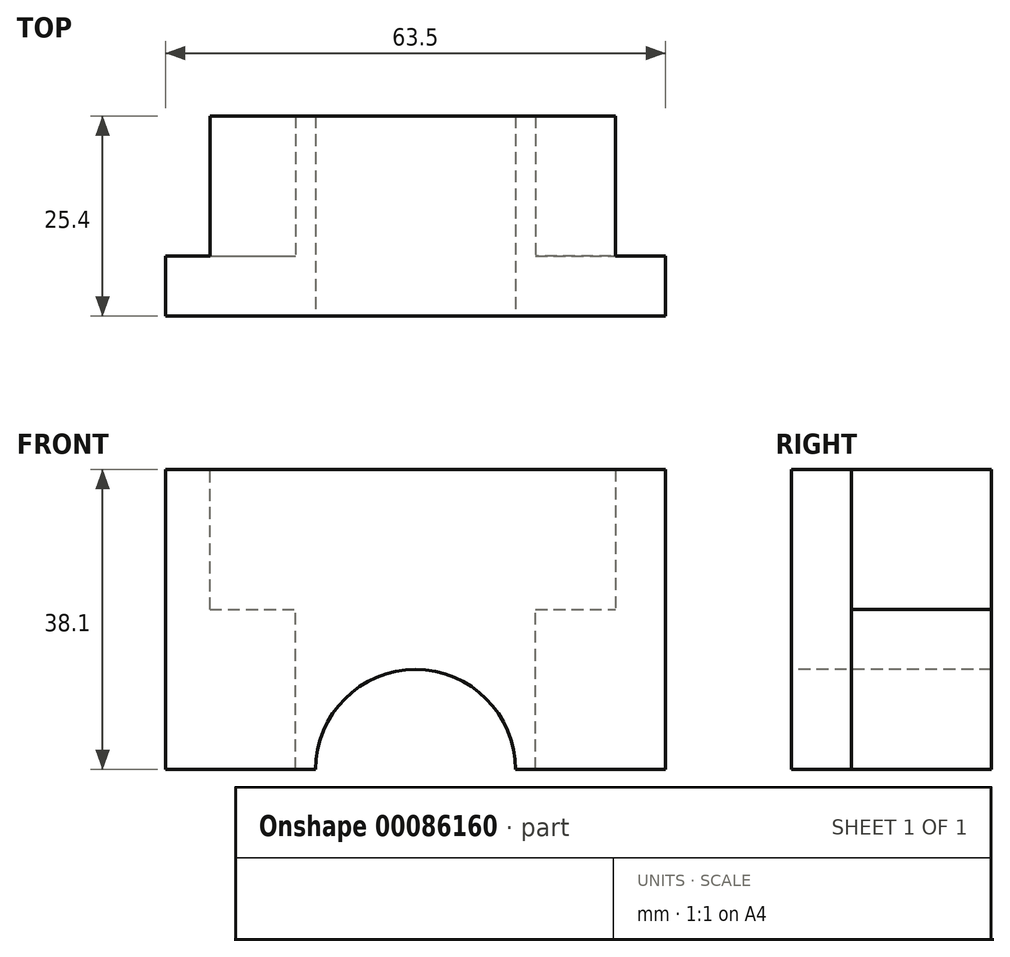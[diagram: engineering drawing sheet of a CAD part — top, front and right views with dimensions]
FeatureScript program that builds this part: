
annotation { "Feature Type Name" : "Feature", "Feature Type Description" : "" }
export const myFeature = defineFeature(function(context is Context, id is Id, definition is map)
    precondition{}
    {
        {
            var Q0;
            Q0=qCreatedBy(makeId("Front.planeOp"),FACE);
            var sketch = newSketch(context, id + "F0", { "sketchPlane" : qUnion([Q0])});
            skLineSegment(sketch, "E0", {"start": v(31.13, 18.61) * mm, "end": v(-32.37, 18.61) * mm});
            skLineSegment(sketch, "E1", {"start": v(-32.37, 18.61) * mm, "end": v(-32.37, -19.49) * mm});
            skLineSegment(sketch, "E2", {"start": v(-32.37, -19.49) * mm, "end": v(31.13, -19.49) * mm});
            skLineSegment(sketch, "E3", {"start": v(31.13, 18.61) * mm, "end": v(31.13, -19.49) * mm});
            skSolve(sketch);
        }
        {
            var Q0;
            Q0=makeQuery(id+"F0.imprint","IMPRINT",FACE,{"disambiguationData":[TD([[makeQuery(id+"F0.imprint","IMPRINT",EDGE,{"derivedFrom":sQuery(id+"F0.wireOp",EDGE,"E0")}),1.0]])]});
            extrude(context, id + "F1", {"entities" : qUnion([Q0]), "depth" : 7.62 * mm});
        }
        {
            var Q0;
            Q0=makeQuery(id+"F1.opExtrude","CAP_FACE",FACE,{"disambiguationData":[OSD([sQuery(id+"F0.wireOp",EDGE,"E0"),sQuery(id+"F0.wireOp",EDGE,"E1"),sQuery(id+"F0.wireOp",EDGE,"E2"),sQuery(id+"F0.wireOp",EDGE,"E3")])],"isStart":true});
            extrude(context, id + "F2", {"entities" : qUnion([Q0]), "operationType" : NewBodyOperationType.ADD, "depth" : 17.78 * mm});
        }
        {
            var Q0;
            Q0=qCreatedBy(makeId("Front.planeOp"),FACE);
            var sketch = newSketch(context, id + "F3", { "sketchPlane" : qUnion([Q0])});
            skLineSegment(sketch, "E4.bottom", {"start": v(31.13, 18.61) * mm, "end": v(24.78, 18.61) * mm});
            skLineSegment(sketch, "E4.top", {"start": v(31.13, -19.49) * mm, "end": v(24.78, -19.49) * mm});
            skLineSegment(sketch, "E4.left", {"start": v(31.13, 18.61) * mm, "end": v(31.13, -19.49) * mm});
            skLineSegment(sketch, "E4.right", {"start": v(24.78, 18.61) * mm, "end": v(24.78, -19.49) * mm});
            skLineSegment(sketch, "E5.top", {"start": v(-32.37, 18.61) * mm, "end": v(-26.74, 18.61) * mm});
            skLineSegment(sketch, "E5.left", {"start": v(-32.37, -19.49) * mm, "end": v(-32.37, 18.61) * mm});
            skLineSegment(sketch, "E5.right", {"start": v(-26.74, -19.49) * mm, "end": v(-26.74, 18.61) * mm});
            skLineSegment(sketch, "E6", {"start": v(-32.37, -19.49) * mm, "end": v(-26.74, -19.49) * mm});
            skSolve(sketch);
        }
        {
            var Q0;
            Q0 = qSketchRegion(id + "F3", true);
            extrude(context, id + "F4", {"entities" : qUnion([Q0]), "operationType" : NewBodyOperationType.REMOVE, "oppositeDirection" : true, "depth" : 17.78 * mm});
        }
        {
            var Q0;
            Q0=qCreatedBy(makeId("Front.planeOp"),FACE);
            var sketch = newSketch(context, id + "F5", { "sketchPlane" : qUnion([Q0])});
            skLineSegment(sketch, "E7.bottom", {"start": v(-32.37, -19.49) * mm, "end": v(-15.86, -19.49) * mm});
            skLineSegment(sketch, "E7.top", {"start": v(-32.37, 0.83) * mm, "end": v(-15.86, 0.83) * mm});
            skLineSegment(sketch, "E7.left", {"start": v(-32.37, -19.49) * mm, "end": v(-32.37, 0.83) * mm});
            skLineSegment(sketch, "E7.right", {"start": v(-15.86, -19.49) * mm, "end": v(-15.86, 0.83) * mm});
            skSolve(sketch);
        }
        {
            var Q0;
            Q0 = qSketchRegion(id + "F5", true);
            extrude(context, id + "F6", {"entities" : qUnion([Q0]), "operationType" : NewBodyOperationType.REMOVE, "oppositeDirection" : true, "depth" : 27.92 * mm});
        }
        {
            var Q0;
            Q0=qCreatedBy(makeId("Front.planeOp"),FACE);
            var sketch = newSketch(context, id + "F7", { "sketchPlane" : qUnion([Q0])});
            skLineSegment(sketch, "E8.bottom", {"start": v(14.62, -19.49) * mm, "end": v(31.13, -19.49) * mm});
            skLineSegment(sketch, "E8.top", {"start": v(14.62, 0.83) * mm, "end": v(31.13, 0.83) * mm});
            skLineSegment(sketch, "E8.left", {"start": v(14.62, -19.49) * mm, "end": v(14.62, 0.83) * mm});
            skLineSegment(sketch, "E8.right", {"start": v(31.13, -19.49) * mm, "end": v(31.13, 0.83) * mm});
            skSolve(sketch);
        }
        {
            var Q0;
            Q0 = qSketchRegion(id + "F7", true);
            extrude(context, id + "F8", {"entities" : qUnion([Q0]), "operationType" : NewBodyOperationType.REMOVE, "oppositeDirection" : true, "depth" : 28.7 * mm});
        }
        {
            var Q0;
            Q0=makeQuery(id+"F1.opExtrude","CAP_FACE",FACE,{"disambiguationData":[OSD([sQuery(id+"F0.wireOp",EDGE,"E0"),sQuery(id+"F0.wireOp",EDGE,"E1"),sQuery(id+"F0.wireOp",EDGE,"E2"),sQuery(id+"F0.wireOp",EDGE,"E3")])],"isStart":false});
            var sketch = newSketch(context, id + "F9", { "sketchPlane" : qUnion([Q0])});
            skCircle(sketch, "E9", {"center": v(-0.62, -19.49) * mm, "radius": 12.7 * mm});
            skSolve(sketch);
        }
        {
            var Q0;
            Q0 = qSketchRegion(id + "F9", true);
            extrude(context, id + "F10", {"entities" : qUnion([Q0]), "operationType" : NewBodyOperationType.REMOVE, "oppositeDirection" : true, "depth" : 30.26 * mm});
        }
    });
